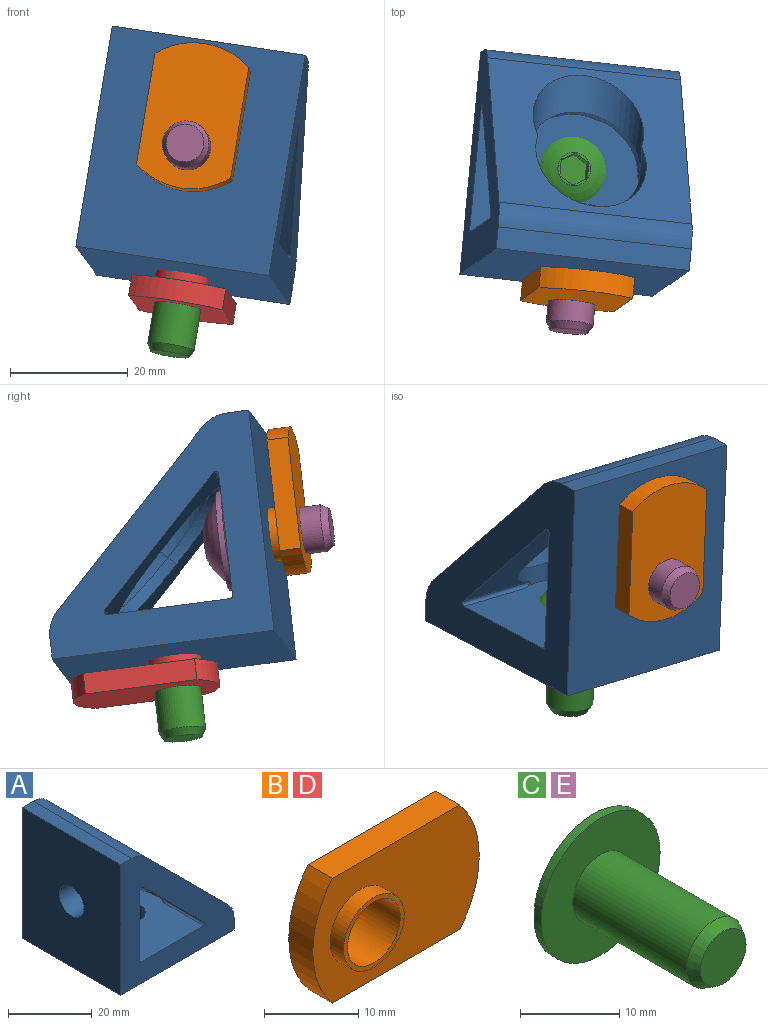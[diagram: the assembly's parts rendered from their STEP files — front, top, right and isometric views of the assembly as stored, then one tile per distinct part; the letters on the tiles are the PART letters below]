
ASSEMBLY  parts=5 mates=4
PART A: 24 faces, bbox 38.1x33.3x38.1 mm
  f0: plane 33.33x28.03mm, normal (0.71,0,0.71), area 750.1mm2, adj f6,f9,f10,f15,f16,f23
  f1: plane 21.04x21.04mm, normal (-0.71,0,-0.71), area 260.3mm2, adj f3,f5,f7,f10,f22
  f2: plane 21.04x21.04mm, normal (-0.71,0,-0.71), area 260.3mm2, adj f4,f5,f8,f9,f22
  f3: cylinder r=0.51mm len=14.85mm, axis (0,1,0), area 17.1mm2, adj f1,f10,f18,f22
  f4: cylinder r=0.51mm len=14.85mm, axis (0,1,0), area 17.1mm2, adj f2,f9,f18,f22
  f5: cylinder r=9.53mm len=19.05mm, axis (-1,0,0), area 84.9mm2, adj f1,f2,f7,f8,f19,f22,f23
  f6: cylinder r=9.53mm len=19.05mm, axis (-1,0,0), area 210.5mm2, adj f0,f22,f23
  f7: cylinder r=0.51mm len=14.85mm, axis (0,1,0), area 17.1mm2, adj f1,f5,f10,f19
  f8: cylinder r=0.51mm len=14.85mm, axis (0,1,0), area 17.1mm2, adj f2,f5,f9,f19
  f9: plane 38.1x38.1mm, normal (0,-1,0), area 687.3mm2, adj f0,f2,f4,f8,f11,f12,f13,f14
  f10: plane 38.1x38.1mm, normal (0,1,0), area 687.3mm2, adj f0,f1,f3,f7,f11,f12,f13,f14
  f11: plane 33.33x3.72mm, normal (0,0,1), area 124mm2, adj f9,f10,f12,f16
  f12: plane 38.1x33.33mm, normal (-1,0,0), area 1215.1mm2, adj f9,f10,f11,f13,f20
  f13: plane 38.1x33.33mm, normal (0,0,-1), area 1215.2mm2, adj f9,f10,f12,f14,f21
  f14: plane 33.33x3.72mm, normal (1,0,0), area 124mm2, adj f9,f10,f13,f15
  f15: cylinder r=6.35mm len=33.33mm, axis (0,1,0), area 166.2mm2, adj f0,f9,f10,f14
  f16: cylinder r=6.35mm len=33.33mm, axis (0,1,0), area 166.2mm2, adj f0,f9,f10,f11
  f17: cylinder r=0.51mm len=33.33mm, axis (0,1,0), area 26.6mm2, adj f9,f10,f18,f19
  f18: plane 33.33x21.72mm, normal (0,0,1), area 649.7mm2, adj f3,f4,f9,f10,f17,f21,f22
  f19: plane 33.33x21.72mm, normal (1,0,0), area 649.6mm2, adj f5,f7,f8,f9,f10,f17,f20
  f20: cylinder r=4.17mm len=8.34mm, axis (-1,0,0), area 166.4mm2, adj f12,f19
  f21: cylinder r=4.17mm len=8.33mm, axis (0,0,-1), area 166.2mm2, adj f13,f18
  f22: cylinder r=9.53mm len=19.05mm, axis (0,0,-1), area 84.9mm2, adj f1,f2,f3,f4,f5,f6,f18
  f23: cylinder r=9.53mm len=19.05mm, axis (0,0,-1), area 210.5mm2, adj f0,f5,f6
PART B: 9 faces, bbox 25x5.6x16.2 mm
  f0: cylinder r=12.7mm len=16.21mm, axis (0,-1,0), area 63.4mm2, adj f1,f3,f4,f5
  f1: plane 19.15x3.61mm, normal (0,0,-1), area 69.1mm2, adj f0,f2,f4,f5
  f2: cylinder r=12.7mm len=16.21mm, axis (0,-1,0), area 63.4mm2, adj f1,f3,f4,f5
  f3: plane 19.15x3.61mm, normal (0,0,1), area 69.1mm2, adj f0,f2,f4,f5
  f4: plane 24.99x16.21mm, normal (0,1,0), area 325.6mm2, adj f0,f1,f2,f3,f8
  f5: plane 24.99x16.21mm, normal (0,-1,0), area 309.8mm2, adj f0,f1,f2,f3,f6
  f6: cylinder r=4.56mm len=9.12mm, axis (0,-1,0), area 58.2mm2, adj f5,f7
  f7: plane 9.12x9.12mm, normal (0,-1,0), area 15.8mm2, adj f6,f8
  f8: cylinder r=3.97mm len=7.94mm, axis (0,1,0), area 140.6mm2, adj f4,f7
PART C: 15 faces, bbox 16.9x21.6x16.9 mm
  f0: plane 16.93x16.93mm, normal (0,-1,0), area 175.7mm2, adj f3,f12
  f1: sphere r=9.06mm, area 176.6mm2, adj f2,f4
  f2: plane 5.66x5.66mm, normal (0,1,0), area 5.5mm2, adj f1,f5,f6,f7,f8,f9,f10
  f3: cylinder r=8.47mm len=16.93mm, axis (0,-1,0), area 55mm2, adj f0,f4
  f4: plane 16.93x16.93mm, normal (0,1,0), area 62.5mm2, adj f1,f3
  f5: plane 2.54x2.38mm, normal (0.87,0,0.5), area 7mm2, adj f2,f6,f10,f11
  f6: plane 2.75x2.54mm, normal (0,0,1), area 7mm2, adj f2,f5,f7,f11
  f7: plane 2.54x2.38mm, normal (-0.87,0,0.5), area 7mm2, adj f2,f6,f8,f11
  f8: plane 2.54x2.38mm, normal (-0.87,0,-0.5), area 7mm2, adj f2,f7,f9,f11
  f9: plane 2.75x2.54mm, normal (0,0,-1), area 7mm2, adj f2,f8,f10,f11
  f10: plane 2.54x2.38mm, normal (0.87,0,-0.5), area 7mm2, adj f2,f5,f9,f11
  f11: plane 5.5x4.76mm, normal (0,1,0), area 19.6mm2, adj f5,f6,f7,f8,f9,f10
  f12: cylinder r=3.97mm len=16.19mm, axis (0,1,0), area 403.8mm2, adj f0,f14
  f13: plane 6.47x6.47mm, normal (0,-1,0), area 32.9mm2, adj f14
  f14: cone r=3.24mm half-angle=30deg, axis (0,1,0), area 33.2mm2, adj f12,f13
PART D: same geometry as B
PART E: same geometry as C
PLACE A rot(axis=(-0.67,-0.53,-0.52),122.6deg) t=(-129.51,564.06,-280.95)mm
PLACE B rot(axis=(0.76,0.01,0.65),170.9deg) t=(-125.89,563.37,-256.57)mm
PLACE C rot(axis=(0.62,0.63,0.47),118.2deg) t=(-126.45,583.77,-275.61)mm
PLACE D rot(axis=(-0.61,-0.47,0.64),115.8deg) t=(-127.8,587.77,-287.5)mm
PLACE E rot(axis=(-0.54,0.7,-0.46),12.8deg) t=(-125.36,577.54,-263.75)mm
MATE slider B.f6 <-> E.f12  axis (-0.09,-0.99,0.13) through (-126.92,560.99,-261.59)mm
MATE slider C.f12 <-> A.f20  axis (0.16,0.11,0.98) through (-127.12,583.3,-279.66)mm
MATE slider E.f12 <-> A.f21  axis (0.09,0.99,-0.13) through (-125.75,573.46,-263.22)mm
MATE slider D.f6 <-> C.f12  axis (-0.16,-0.11,-0.98) through (-128.59,582.28,-288.58)mm
